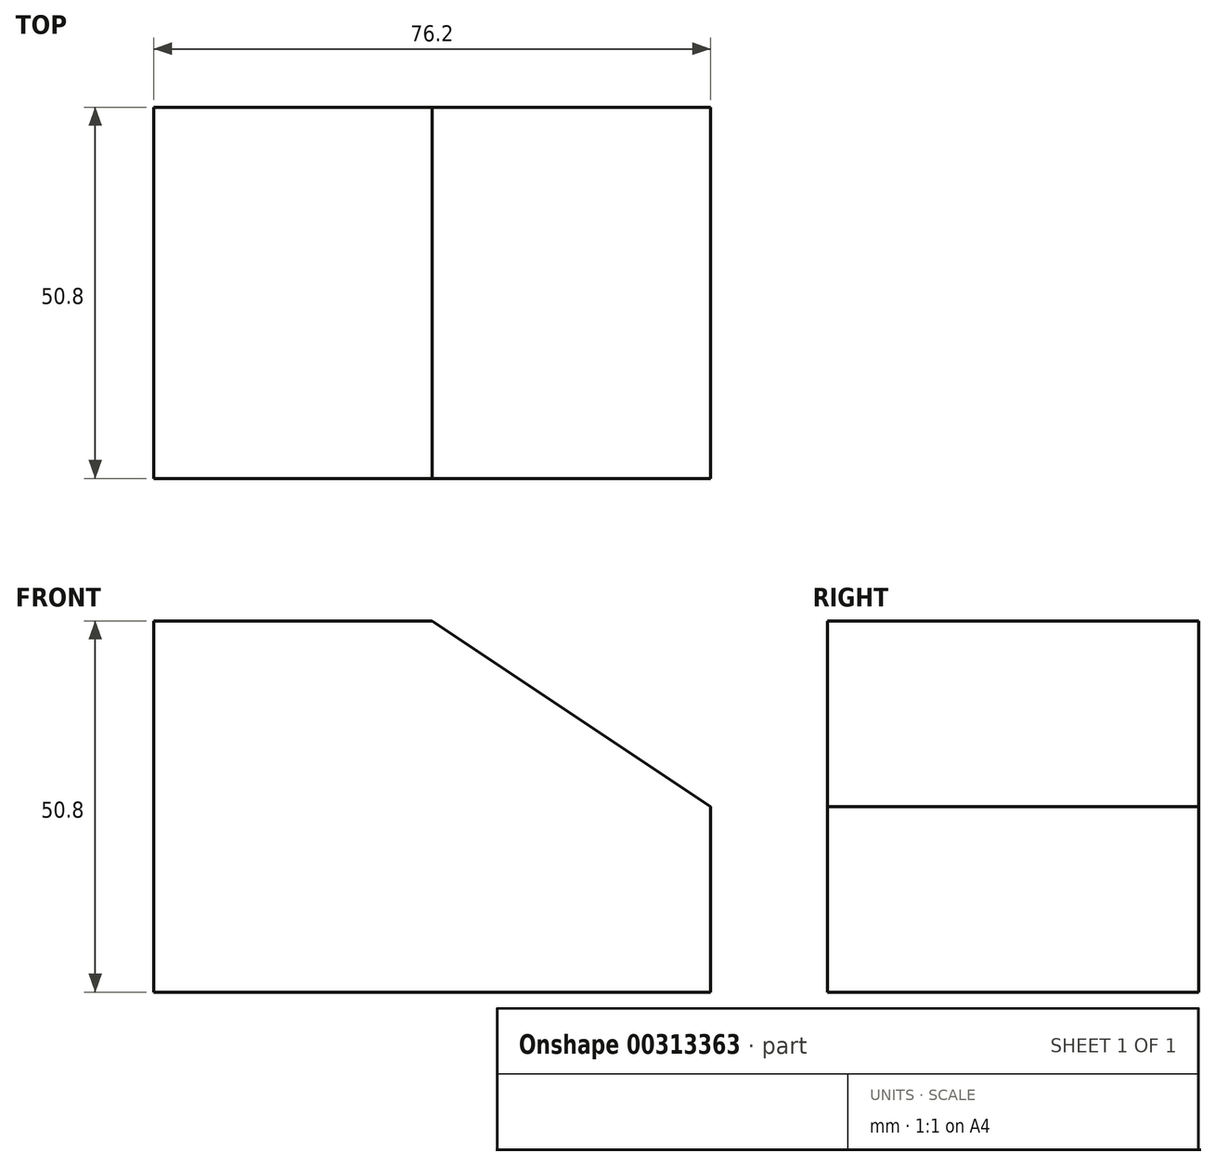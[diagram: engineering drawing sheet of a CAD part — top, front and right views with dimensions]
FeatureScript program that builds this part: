
annotation { "Feature Type Name" : "Feature", "Feature Type Description" : "" }
export const myFeature = defineFeature(function(context is Context, id is Id, definition is map)
    precondition{}
    {
        {
            var Q0;
            Q0=qCreatedBy(makeId("Front.planeOp"),FACE);
            var sketch = newSketch(context, id + "F0", { "sketchPlane" : qUnion([Q0])});
            skLineSegment(sketch, "E0", {"start": v(-35.26, -18.64) * mm, "end": v(40.94, -18.64) * mm});
            skLineSegment(sketch, "E1", {"start": v(40.94, -18.64) * mm, "end": v(40.94, 6.76) * mm});
            skLineSegment(sketch, "E2", {"start": v(40.94, 6.76) * mm, "end": v(2.84, 32.16) * mm});
            skLineSegment(sketch, "E3", {"start": v(2.84, 32.16) * mm, "end": v(-35.26, 32.16) * mm});
            skLineSegment(sketch, "E4", {"start": v(-35.26, 32.16) * mm, "end": v(-35.26, -18.64) * mm});
            skSolve(sketch);
        }
        {
            var Q0;
            Q0=makeQuery(id+"F0.imprint","IMPRINT",FACE,{"disambiguationData":[TD([[makeQuery(id+"F0.imprint","IMPRINT",EDGE,{"derivedFrom":sQuery(id+"F0.wireOp",EDGE,"E0")}),1.0]])]});
            extrude(context, id + "F1", {"entities" : qUnion([Q0]), "depth" : 50.8 * mm});
        }
    });
